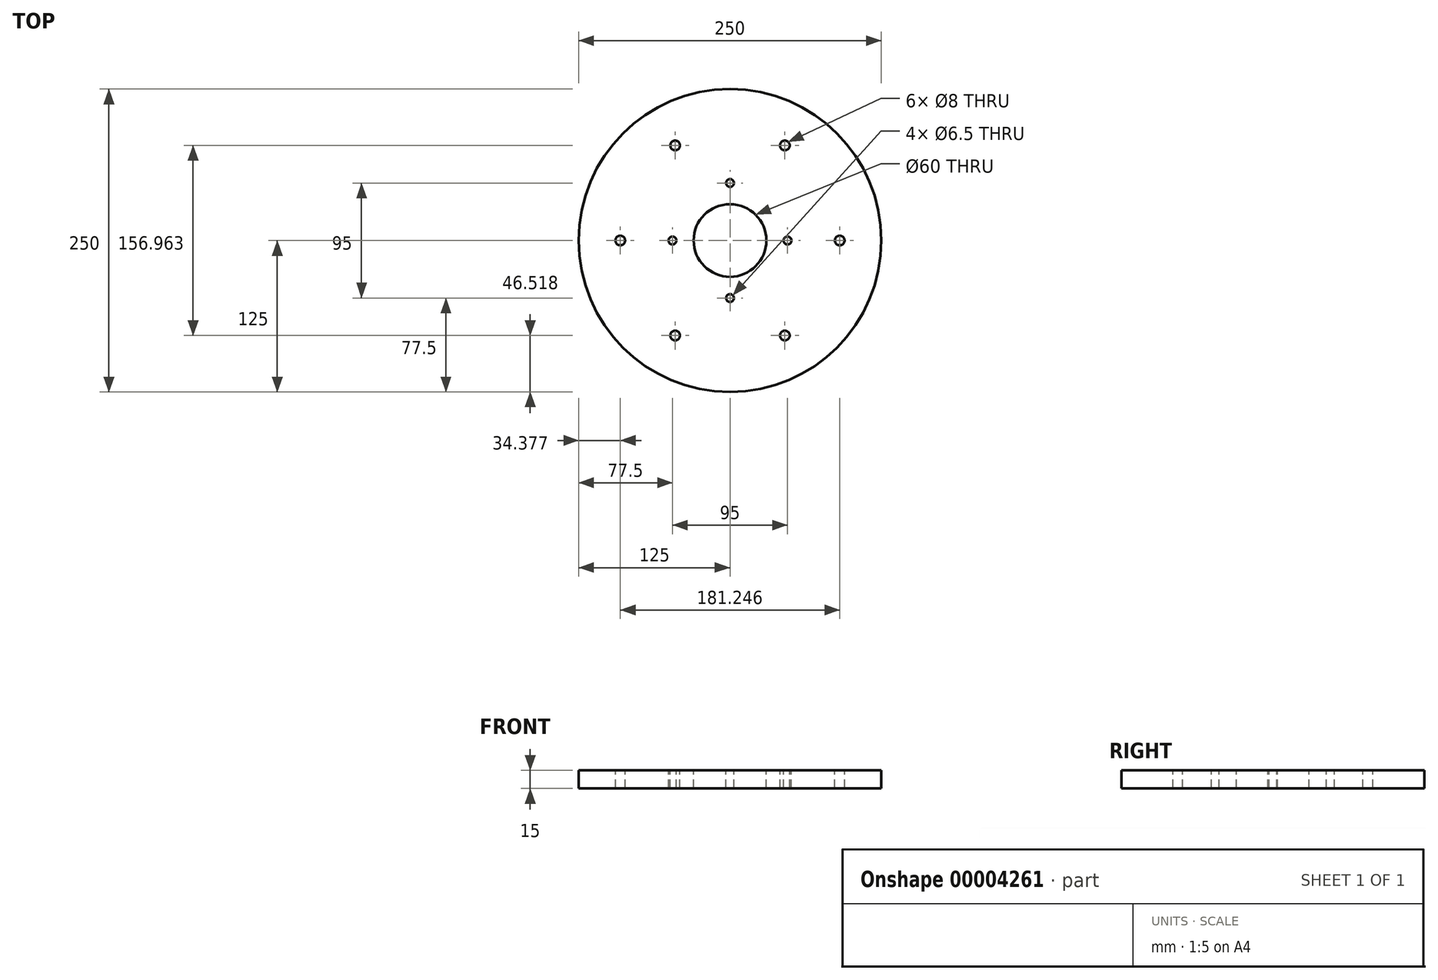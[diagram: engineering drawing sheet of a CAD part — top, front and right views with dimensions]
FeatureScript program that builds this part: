
annotation { "Feature Type Name" : "Feature", "Feature Type Description" : "" }
export const myFeature = defineFeature(function(context is Context, id is Id, definition is map)
    precondition{}
    {
        {
            var Q0;
            Q0=qCreatedBy(makeId("Top.planeOp"),FACE);
            var sketch = newSketch(context, id + "F0", { "sketchPlane" : qUnion([Q0])});
            skCircle(sketch, "E0", {"center": v(0, 0) * mm, "radius": 125 * mm});
            skSolve(sketch);
        }
        {
            var Q0;
            Q0=makeQuery(id+"F0.imprint","IMPRINT",FACE,{"disambiguationData":[TD([[makeQuery(id+"F0.imprint","IMPRINT",EDGE,{"derivedFrom":sQuery(id+"F0.wireOp",EDGE,"E0")}),1.0]])]});
            extrude(context, id + "F1", {"entities" : qUnion([Q0]), "depth" : 15 * mm});
        }
        {
            var Q0;
            Q0=makeQuery(id+"F1.opExtrude","CAP_FACE",FACE,{"disambiguationData":[OSD([sQuery(id+"F0.wireOp",EDGE,"E0")])],"isStart":false});
            var sketch = newSketch(context, id + "F2", { "sketchPlane" : qUnion([Q0])});
            skCircle(sketch, "E1", {"center": v(0, 0) * mm, "radius": 30 * mm});
            skSolve(sketch);
        }
        {
            var Q0;
            Q0=makeQuery(id+"F2.imprint","IMPRINT",FACE,{"disambiguationData":[TD([[makeQuery(id+"F2.imprint","IMPRINT",EDGE,{"derivedFrom":sQuery(id+"F2.wireOp",EDGE,"E1")}),1.0]])]});
            extrude(context, id + "F3", {"entities" : qUnion([Q0]), "operationType" : NewBodyOperationType.REMOVE, "endBound" : BoundingType.THROUGH_ALL, "oppositeDirection" : true, "depth" : 25 * mm});
        }
        {
            var Q0;
            Q0=makeQuery(id+"F1.opExtrude","CAP_FACE",FACE,{"disambiguationData":[OSD([sQuery(id+"F0.wireOp",EDGE,"E0")])],"isStart":false});
            var sketch = newSketch(context, id + "F4", { "sketchPlane" : qUnion([Q0])});
            skCircle(sketch, "E2", {"center": v(0, 0) * mm, "radius": 47.5 * mm, "construction": true});
            skCircle(sketch, "E3", {"center": v(0, 47.5) * mm, "radius": 3.25 * mm});
            skCircle(sketch, "E4.1.0", {"center": v(-47.5, 0) * mm, "radius": 3.25 * mm});
            skCircle(sketch, "E4.2.0", {"center": v(0, -47.5) * mm, "radius": 3.25 * mm});
            skCircle(sketch, "E4.3.0", {"center": v(47.5, 0) * mm, "radius": 3.25 * mm});
            skCircle(sketch, "E5", {"center": v(0, 0) * mm, "radius": 90.62 * mm, "construction": true});
            skCircle(sketch, "E6", {"center": v(90.62, 0) * mm, "radius": 4 * mm});
            skCircle(sketch, "E7.1.0", {"center": v(45.31, 78.48) * mm, "radius": 4 * mm});
            skCircle(sketch, "E7.2.0", {"center": v(-45.31, 78.48) * mm, "radius": 4 * mm});
            skCircle(sketch, "E7.3.0", {"center": v(-90.62, 0) * mm, "radius": 4 * mm});
            skCircle(sketch, "E7.4.0", {"center": v(-45.31, -78.48) * mm, "radius": 4 * mm});
            skCircle(sketch, "E7.5.0", {"center": v(45.31, -78.48) * mm, "radius": 4 * mm});
            skSolve(sketch);
        }
        {
            var Q0;
            Q0=makeQuery(id+"F4.imprint","IMPRINT",FACE,{"disambiguationData":[TD([[makeQuery(id+"F4.imprint","IMPRINT",EDGE,{"derivedFrom":sQuery(id+"F4.wireOp",EDGE,"E3")}),1.0]])]});
            var Q1;
            Q1=makeQuery(id+"F4.imprint","IMPRINT",FACE,{"disambiguationData":[TD([[makeQuery(id+"F4.imprint","IMPRINT",EDGE,{"derivedFrom":sQuery(id+"F4.wireOp",EDGE,"E4.1.0")}),1.0]])]});
            var Q2;
            Q2=makeQuery(id+"F4.imprint","IMPRINT",FACE,{"disambiguationData":[TD([[makeQuery(id+"F4.imprint","IMPRINT",EDGE,{"derivedFrom":sQuery(id+"F4.wireOp",EDGE,"E4.2.0")}),1.0]])]});
            var Q3;
            Q3=makeQuery(id+"F4.imprint","IMPRINT",FACE,{"disambiguationData":[TD([[makeQuery(id+"F4.imprint","IMPRINT",EDGE,{"derivedFrom":sQuery(id+"F4.wireOp",EDGE,"E4.3.0")}),1.0]])]});
            extrude(context, id + "F5", {"entities" : qUnion([Q0, Q1, Q2, Q3]), "operationType" : NewBodyOperationType.REMOVE, "endBound" : BoundingType.THROUGH_ALL, "oppositeDirection" : true, "depth" : 25 * mm});
        }
        {
            var Q0;
            Q0 = qSketchRegion(id + "F4", true);
            extrude(context, id + "F6", {"entities" : qUnion([Q0]), "operationType" : NewBodyOperationType.REMOVE, "endBound" : BoundingType.THROUGH_ALL, "oppositeDirection" : true, "depth" : 25 * mm});
        }
    });
